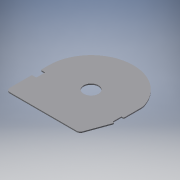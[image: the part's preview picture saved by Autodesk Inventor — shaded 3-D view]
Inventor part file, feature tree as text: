
AUTODESK INVENTOR PART (.ipt)
format: ipt  version: 2016 (Build 200138000, 138)  size: 151,552 bytes
history: native  units: mm
features: fillet x3, extrude x1, sketch x1
ambient origin geometry x8: Origin, YZ Plane, XZ Plane, XY Plane, X Axis, Y Axis, Z Axis, Center Point
bodies: Solid1 (feature_tree)
feature tree (5):
  extrude  "Extrusion1"  Depth=57.0mm
  fillet  "Fillet1"  Radius=20.0mm
  fillet  "Fillet2"  Radius=99.0mm
  fillet  "Fillet3"  Radius=6.0mm
  sketch  "Sketch1"  dims[d0=20.0mm d1=57.0mm d2=20.0mm d3=99.0mm d4=6.0mm d5=19.198622mm d6=3.0mm d7=12.0mm d8=58.0mm d9=12.0mm d10=55.0mm d11=47.0mm d12=1.5mm d13=0.0mm d14=0.5mm d15=1.0mm d16=5.0mm]
